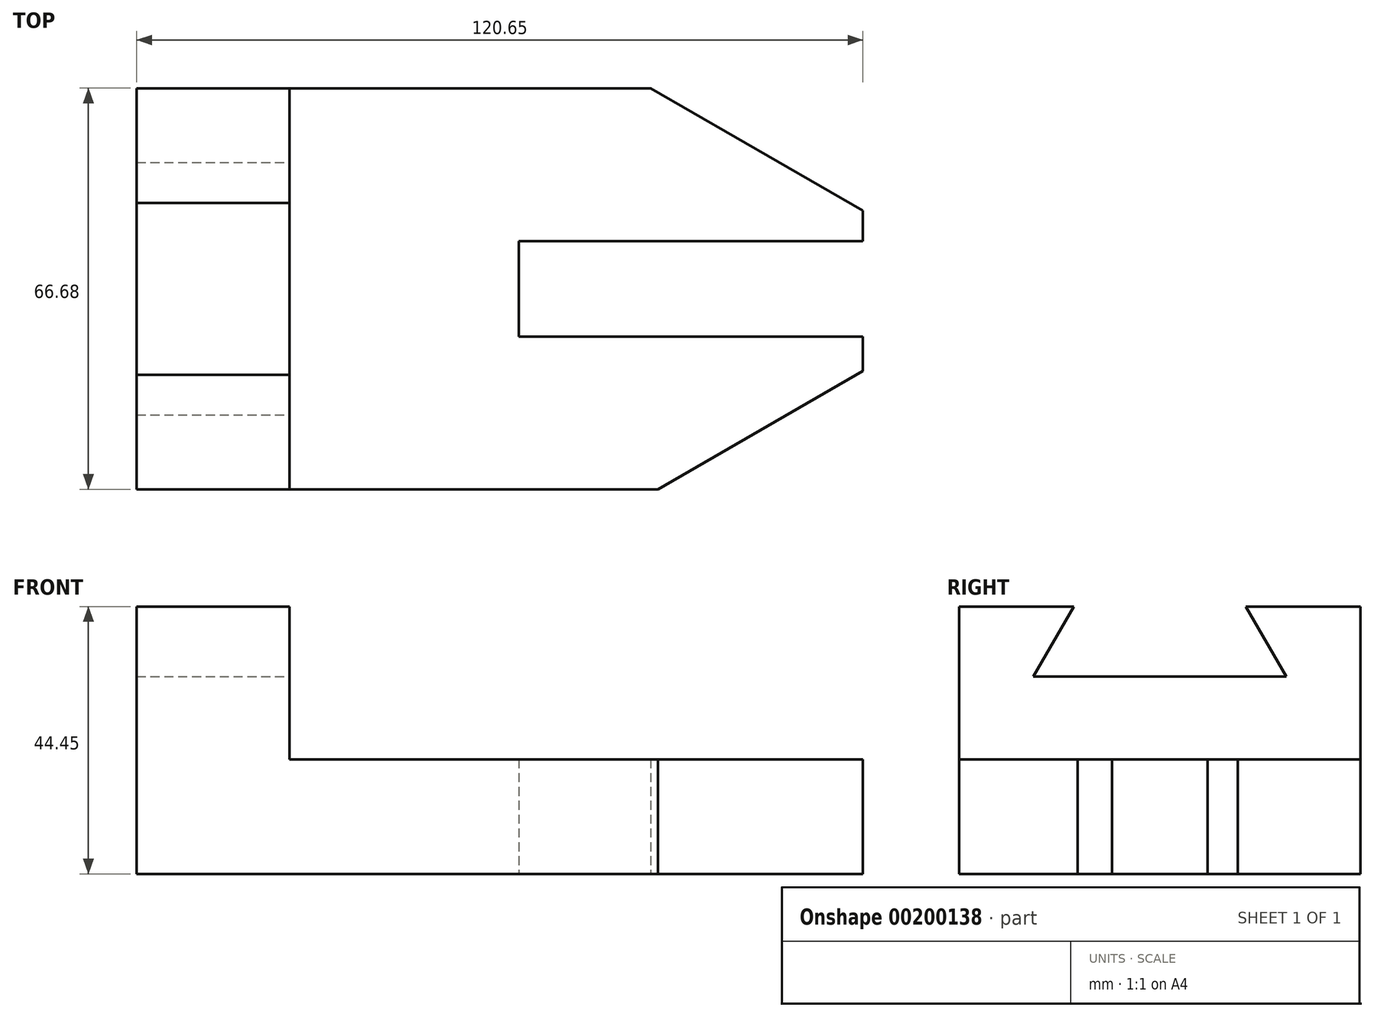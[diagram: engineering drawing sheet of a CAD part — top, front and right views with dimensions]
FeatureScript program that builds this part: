
annotation { "Feature Type Name" : "Feature", "Feature Type Description" : "" }
export const myFeature = defineFeature(function(context is Context, id is Id, definition is map)
    precondition{}
    {
        {
            var Q0;
            Q0=qCreatedBy(makeId("Top.planeOp"),FACE);
            var sketch = newSketch(context, id + "F0", { "sketchPlane" : qUnion([Q0])});
            skLineSegment(sketch, "E0.bottom", {"start": v(-32, 34.76) * mm, "end": v(53.38, 34.76) * mm});
            skLineSegment(sketch, "E0.top", {"start": v(-32, -31.92) * mm, "end": v(54.58, -31.92) * mm});
            skLineSegment(sketch, "E0.left", {"start": v(-32, 34.76) * mm, "end": v(-32, -31.92) * mm});
            skLineSegment(sketch, "E0.right", {"start": v(88.66, 14.39) * mm, "end": v(88.66, 9.36) * mm});
            skLineSegment(sketch, "E1", {"start": v(88.66, -12.25) * mm, "end": v(54.58, -31.92) * mm});
            skLineSegment(sketch, "E2", {"start": v(53.38, 34.76) * mm, "end": v(88.66, 14.39) * mm});
            skLineSegment(sketch, "E3.bottom", {"start": v(88.66, 9.36) * mm, "end": v(31.5, 9.36) * mm});
            skLineSegment(sketch, "E3.top", {"start": v(88.66, -6.52) * mm, "end": v(31.5, -6.52) * mm});
            skLineSegment(sketch, "E3.right", {"start": v(31.5, 9.36) * mm, "end": v(31.5, -6.52) * mm});
            skPoint(sketch, "E4.orphan", {"position": v(88.66, -31.92) * mm});
            skPoint(sketch, "E5.orphan", {"position": v(88.66, 34.76) * mm});
            skLineSegment(sketch, "E6.trimOffspring", {"start": v(88.66, -6.52) * mm, "end": v(88.66, -12.25) * mm});
            skSolve(sketch);
        }
        {
            var Q0;
            Q0=makeQuery(id+"F0.imprint","IMPRINT",FACE,{"disambiguationData":[TD([[makeQuery(id+"F0.imprint","IMPRINT",EDGE,{"derivedFrom":sQuery(id+"F0.wireOp",EDGE,"E0.bottom")}),-1.0]])]});
            extrude(context, id + "F1", {"entities" : qUnion([Q0]), "depth" : 19.05 * mm});
        }
        {
            var Q0;
            Q0=makeQuery(id+"F1.opExtrude","CAP_FACE",FACE,{"disambiguationData":[OSD([sQuery(id+"F0.wireOp",EDGE,"E0.bottom"),sQuery(id+"F0.wireOp",EDGE,"E0.top"),sQuery(id+"F0.wireOp",EDGE,"E0.left"),sQuery(id+"F0.wireOp",EDGE,"E0.right"),sQuery(id+"F0.wireOp",EDGE,"E1"),sQuery(id+"F0.wireOp",EDGE,"E2"),sQuery(id+"F0.wireOp",EDGE,"E3.bottom"),sQuery(id+"F0.wireOp",EDGE,"E3.top"),sQuery(id+"F0.wireOp",EDGE,"E3.right"),sQuery(id+"F0.wireOp",EDGE,"E6.trimOffspring")])],"isStart":false});
            var sketch = newSketch(context, id + "F2", { "sketchPlane" : qUnion([Q0])});
            skLineSegment(sketch, "E7.bottom", {"start": v(-32, 34.76) * mm, "end": v(-6.6, 34.76) * mm});
            skLineSegment(sketch, "E7.top", {"start": v(-32, -31.92) * mm, "end": v(-6.6, -31.92) * mm});
            skLineSegment(sketch, "E7.left", {"start": v(-32, 34.76) * mm, "end": v(-32, -31.92) * mm});
            skLineSegment(sketch, "E7.right", {"start": v(-6.6, 34.76) * mm, "end": v(-6.6, -31.92) * mm});
            skSolve(sketch);
        }
        {
            var Q0;
            Q0=makeQuery(id+"F2.imprint","IMPRINT",FACE,{"disambiguationData":[TD([[makeQuery(id+"F2.imprint","IMPRINT",EDGE,{"derivedFrom":sQuery(id+"F2.wireOp",EDGE,"E7.bottom")}),-1.0]])]});
            extrude(context, id + "F3", {"entities" : qUnion([Q0]), "operationType" : NewBodyOperationType.ADD, "depth" : 25.4 * mm});
        }
        {
            var Q0;
            Q0=makeQuery(id+"F3.opExtrude","SWEPT_FACE",FACE,{"disambiguationData":[OSD([sQuery(id+"F2.wireOp",EDGE,"E7.right")])]});
            var sketch = newSketch(context, id + "F4", { "sketchPlane" : qUnion([Q0])});
            skLineSegment(sketch, "E8.bottom", {"start": v(-12.87, 44.45) * mm, "end": v(15.7, 44.45) * mm});
            skLineSegment(sketch, "E8.top", {"start": v(-19.58, 32.83) * mm, "end": v(22.41, 32.83) * mm});
            skLineSegment(sketch, "E9", {"start": v(-19.58, 32.83) * mm, "end": v(-12.87, 44.45) * mm});
            skLineSegment(sketch, "E10", {"start": v(15.7, 44.45) * mm, "end": v(22.41, 32.83) * mm});
            skSolve(sketch);
        }
        {
            var Q0;
            Q0=makeQuery(id+"F4.imprint","IMPRINT",FACE,{"disambiguationData":[TD([[makeQuery(id+"F4.imprint","IMPRINT",EDGE,{"derivedFrom":sQuery(id+"F4.wireOp",EDGE,"E8.bottom")}),1.0]])]});
            extrude(context, id + "F5", {"entities" : qUnion([Q0]), "operationType" : NewBodyOperationType.REMOVE, "oppositeDirection" : true, "depth" : 32.26 * mm});
        }
    });
